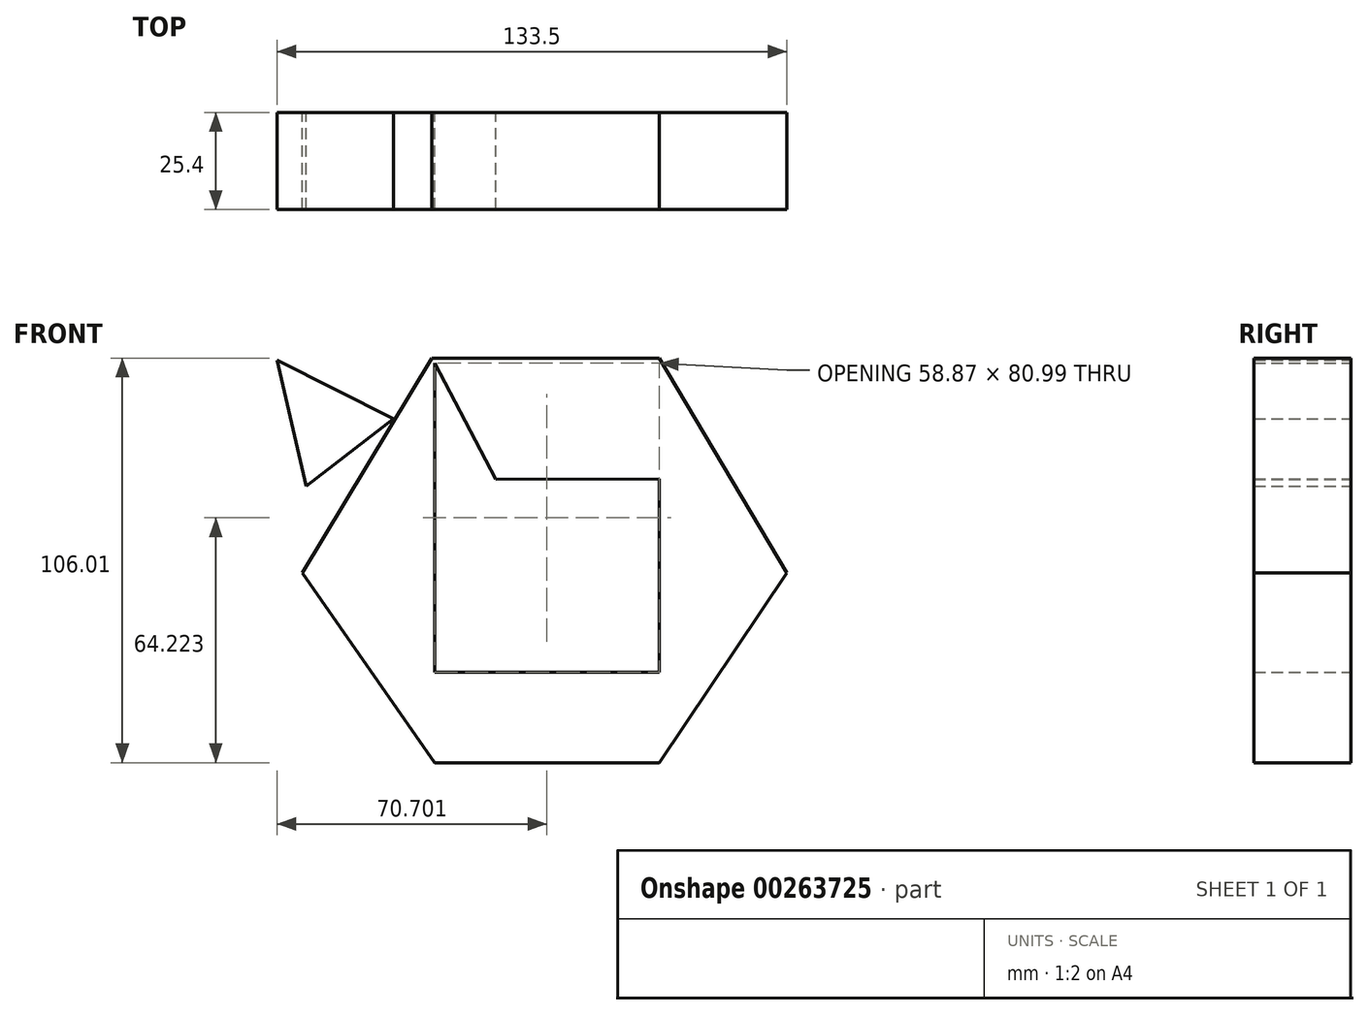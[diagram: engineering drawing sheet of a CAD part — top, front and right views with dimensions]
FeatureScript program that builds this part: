
annotation { "Feature Type Name" : "Feature", "Feature Type Description" : "" }
export const myFeature = defineFeature(function(context is Context, id is Id, definition is map)
    precondition{}
    {
        {
            var Q0;
            Q0=qCreatedBy(makeId("Front.planeOp"),FACE);
            var sketch = newSketch(context, id + "F0", { "sketchPlane" : qUnion([Q0])});
            skLineSegment(sketch, "E0", {"start": v(0, 0) * mm, "end": v(29.86, 56.23) * mm});
            skLineSegment(sketch, "E1", {"start": v(0, 0) * mm, "end": v(-29.68, 56.23) * mm});
            skLineSegment(sketch, "E2", {"start": v(-29, 54.94) * mm, "end": v(-29, -49.78) * mm});
            skLineSegment(sketch, "E3", {"start": v(-29, -49.78) * mm, "end": v(29.86, -49.78) * mm});
            skLineSegment(sketch, "E4", {"start": v(29.86, -49.78) * mm, "end": v(29.86, 56.23) * mm});
            skLineSegment(sketch, "E5", {"start": v(29.86, 56.23) * mm, "end": v(63.23, 0) * mm});
            skLineSegment(sketch, "E6", {"start": v(63.23, 0) * mm, "end": v(29.86, -49.78) * mm});
            skLineSegment(sketch, "E7", {"start": v(-29, -49.78) * mm, "end": v(-63.6, 0) * mm});
            skLineSegment(sketch, "E8", {"start": v(-63.6, 0) * mm, "end": v(-29.68, 56.23) * mm});
            skLineSegment(sketch, "E9", {"start": v(-29.68, 56.23) * mm, "end": v(29.86, 56.23) * mm});
            skLineSegment(sketch, "E10", {"start": v(48.55, 24.74) * mm, "end": v(-45.5, -26.05) * mm});
            skLineSegment(sketch, "E11", {"start": v(-45.5, -26.05) * mm, "end": v(45.77, -26.05) * mm});
            skLineSegment(sketch, "E12", {"start": v(45.77, -26.05) * mm, "end": v(-48.97, 24.26) * mm});
            skLineSegment(sketch, "E13", {"start": v(-48.97, 24.26) * mm, "end": v(48.55, 24.74) * mm});
            skSolve(sketch);
        }
        {
            var Q0;
            Q0 = qSketchRegion(id + "F0", true);
            extrude(context, id + "F1", {"entities" : qUnion([Q0]), "depth" : 25.4 * mm});
        }
        {
            var Q0;
            Q0=qCreatedBy(makeId("Front.planeOp"),FACE);
            var sketch = newSketch(context, id + "F2", { "sketchPlane" : qUnion([Q0])});
            skLineSegment(sketch, "E14", {"start": v(-64.62, 19.33) * mm, "end": v(-62.66, 22.66) * mm});
            skLineSegment(sketch, "E15", {"start": v(-62.66, 22.66) * mm, "end": v(-39.8, 40.34) * mm});
            skLineSegment(sketch, "E16", {"start": v(-39.8, 40.34) * mm, "end": v(-70.27, 55.71) * mm});
            skLineSegment(sketch, "E17", {"start": v(-70.27, 55.71) * mm, "end": v(-62.66, 22.66) * mm});
            skSolve(sketch);
        }
        {
            var Q0;
            Q0=makeQuery(id+"F2.imprint","IMPRINT",FACE,{"disambiguationData":[TD([[makeQuery(id+"F2.imprint","IMPRINT",EDGE,{"derivedFrom":sQuery(id+"F2.wireOp",EDGE,"E15")}),1.0]])]});
            extrude(context, id + "F3", {"entities" : qUnion([Q0]), "depth" : 25.4 * mm});
        }
    });
